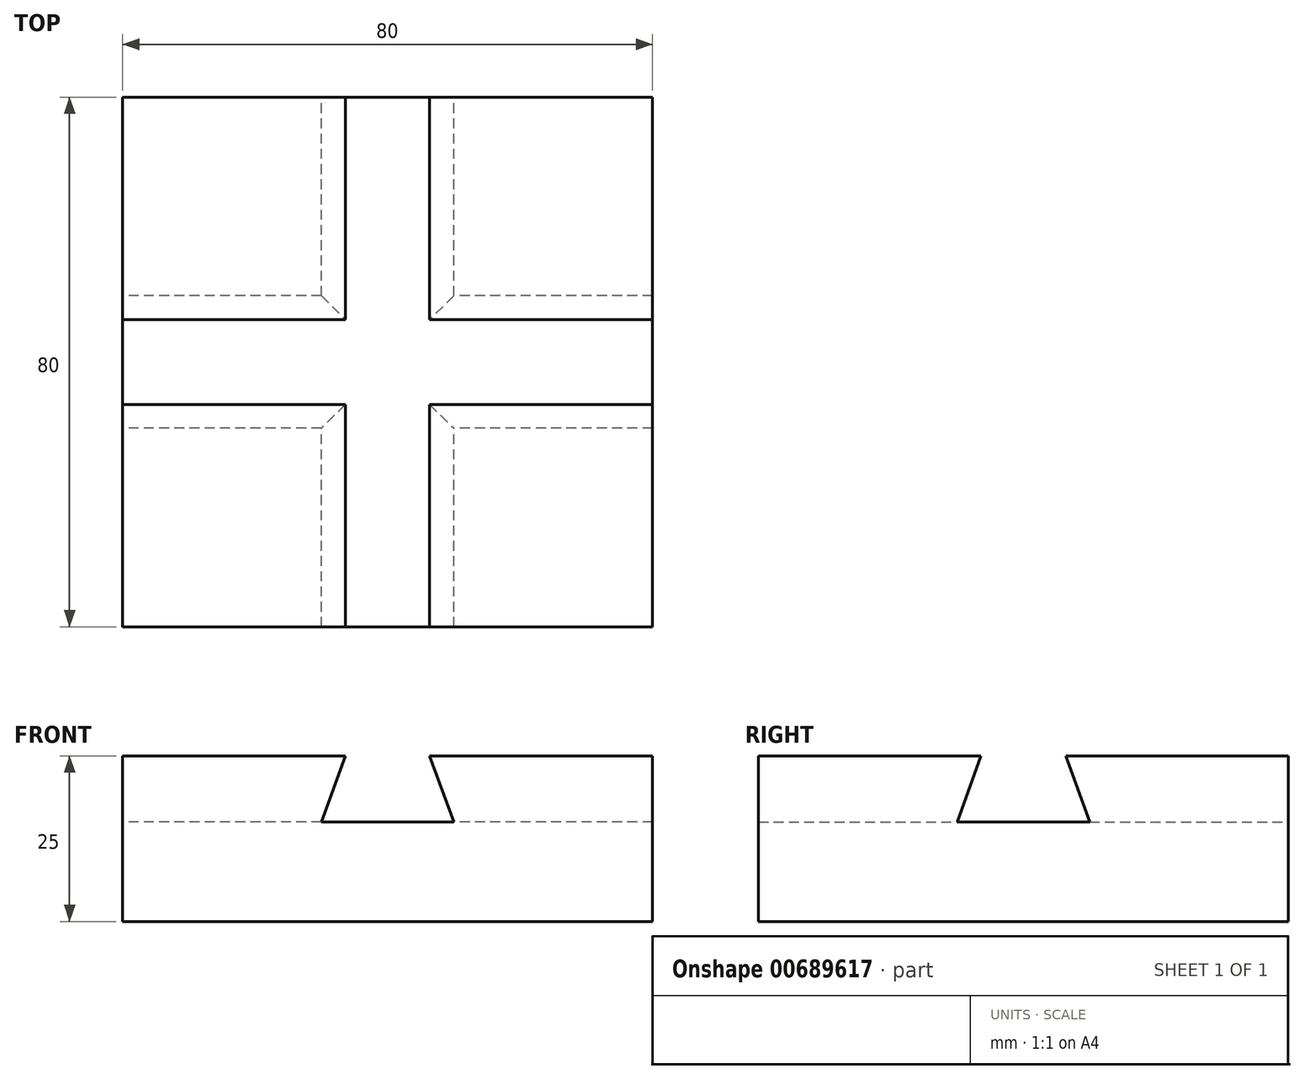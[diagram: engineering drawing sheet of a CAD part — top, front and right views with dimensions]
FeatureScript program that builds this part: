
annotation { "Feature Type Name" : "Feature", "Feature Type Description" : "" }
export const myFeature = defineFeature(function(context is Context, id is Id, definition is map)
    precondition{}
    {
        {
            var Q0;
            Q0=qCreatedBy(makeId("Front.planeOp"),FACE);
            var sketch = newSketch(context, id + "F0", { "sketchPlane" : qUnion([Q0])});
            skLineSegment(sketch, "E0", {"start": v(0, 0) * mm, "end": v(80, 0) * mm});
            skLineSegment(sketch, "E1", {"start": v(0, 0) * mm, "end": v(0, 25) * mm});
            skLineSegment(sketch, "E2", {"start": v(0, 25) * mm, "end": v(33.64, 25) * mm});
            skLineSegment(sketch, "E3", {"start": v(80, 25) * mm, "end": v(80, 0) * mm});
            skLineSegment(sketch, "E4", {"start": v(30, 15) * mm, "end": v(50, 15) * mm});
            skLineSegment(sketch, "E5", {"start": v(30, 15) * mm, "end": v(33.64, 25) * mm});
            skLineSegment(sketch, "E6", {"start": v(50, 15) * mm, "end": v(46.36, 25) * mm});
            skLineSegment(sketch, "E7.trimOffspring", {"start": v(46.36, 25) * mm, "end": v(80, 25) * mm});
            skSolve(sketch);
        }
        {
            var Q0;
            Q0=makeQuery(id+"F0.imprint","IMPRINT",FACE,{"disambiguationData":[TD([[makeQuery(id+"F0.imprint","IMPRINT",EDGE,{"derivedFrom":sQuery(id+"F0.wireOp",EDGE,"E0")}),1.0]])]});
            extrude(context, id + "F1", {"entities" : qUnion([Q0]), "depth" : 80 * mm, "offsetDistance" : 25 * mm});
        }
        {
            var Q0;
            Q0=qCreatedBy(makeId("Right.planeOp"),FACE);
            var sketch = newSketch(context, id + "F2", { "sketchPlane" : qUnion([Q0])});
            skLineSegment(sketch, "E8", {"start": v(-30, 15) * mm, "end": v(-50, 15) * mm});
            skLineSegment(sketch, "E9", {"start": v(-30, 15) * mm, "end": v(-33.64, 25.16) * mm});
            skLineSegment(sketch, "E10", {"start": v(-46.36, 25.16) * mm, "end": v(-50, 15) * mm});
            skLineSegment(sketch, "E11", {"start": v(-33.64, 25.16) * mm, "end": v(-46.36, 25.16) * mm});
            skSolve(sketch);
        }
        {
            var Q0;
            Q0=makeQuery(id+"F2.imprint","IMPRINT",FACE,{"disambiguationData":[TD([[makeQuery(id+"F2.imprint","IMPRINT",EDGE,{"derivedFrom":sQuery(id+"F2.wireOp",EDGE,"E8")}),-1.0]])]});
            extrude(context, id + "F3", {"entities" : qUnion([Q0]), "operationType" : NewBodyOperationType.REMOVE, "depth" : 80 * mm, "offsetDistance" : 25 * mm});
        }
    });
